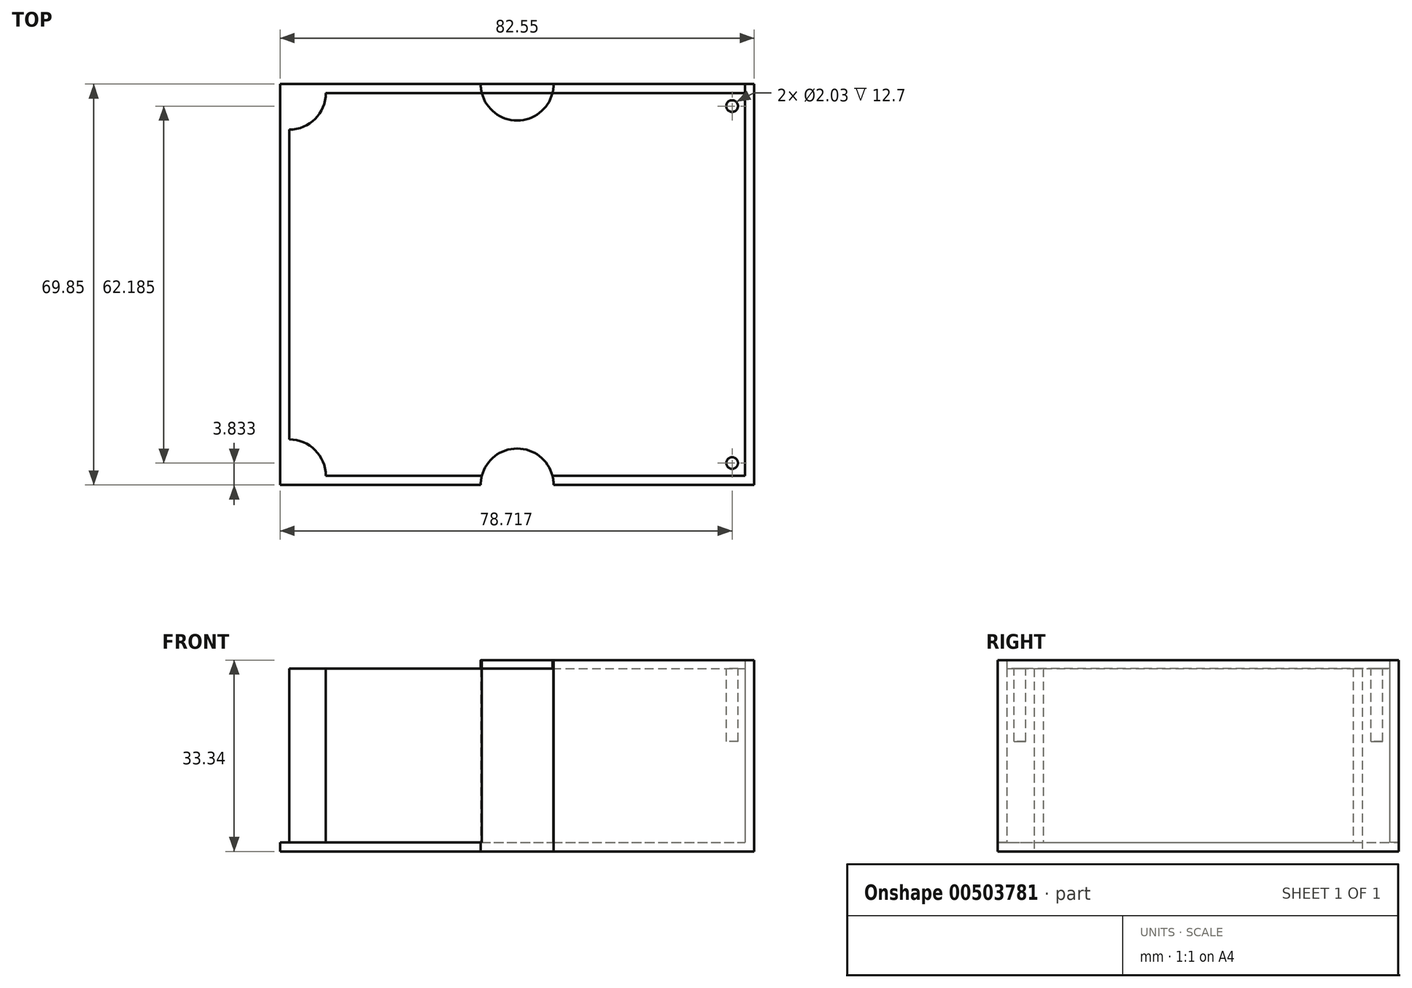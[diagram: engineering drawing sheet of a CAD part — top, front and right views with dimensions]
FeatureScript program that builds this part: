
annotation { "Feature Type Name" : "Feature", "Feature Type Description" : "" }
export const myFeature = defineFeature(function(context is Context, id is Id, definition is map)
    precondition{}
    {
        {
            var Q0;
            Q0=qCreatedBy(makeId("Top.planeOp"),FACE);
            var sketch = newSketch(context, id + "F0", { "sketchPlane" : qUnion([Q0])});
            skLineSegment(sketch, "E0.bottom", {"start": v(0, 0) * mm, "end": v(82.55, 0) * mm});
            skLineSegment(sketch, "E0.top", {"start": v(0, 69.85) * mm, "end": v(82.55, 69.85) * mm});
            skLineSegment(sketch, "E0.left", {"start": v(0, 0) * mm, "end": v(0, 69.85) * mm});
            skLineSegment(sketch, "E0.right", {"start": v(82.55, 0) * mm, "end": v(82.55, 69.85) * mm});
            skCircle(sketch, "E1", {"center": v(41.27, 0) * mm, "radius": 6.35 * mm});
            skCircle(sketch, "E2", {"center": v(41.27, 69.85) * mm, "radius": 6.35 * mm});
            skLineSegment(sketch, "E3", {"start": v(41.27, 69.85) * mm, "end": v(41.27, 76.2) * mm, "construction": true});
            skCircle(sketch, "E4", {"center": v(41.27, 73.02) * mm, "radius": 1.78 * mm});
            skLineSegment(sketch, "E5", {"start": v(41.27, 0) * mm, "end": v(41.27, -6.35) * mm, "construction": true});
            skCircle(sketch, "E6", {"center": v(41.27, -3.18) * mm, "radius": 1.78 * mm});
            skSolve(sketch);
        }
        {
            var Q0;
            Q0=makeQuery(id+"F0.imprint","IMPRINT",FACE,{"disambiguationData":[TD([[makeQuery(id+"F0.imprint","IMPRINT",EDGE,{"derivedFrom":sQuery(id+"F0.wireOp",EDGE,"E0.bottom")}),1.0]])]});
            var Q1;
            {var subQ0=sQuery(id+"F0.wireOp",EDGE,"E2");var subQ1=sQuery(id+"F0.wireOp",EDGE,"E0.top");var subQ2=makeQuery(id+"F0.imprint","INTERSECT",VERTEX,{"disambiguationData":[OD(0.0)],"derivedFrom":[subQ1,subQ0]});Q1=makeQuery(id+"F0.imprint","IMPRINT",FACE,{"disambiguationData":[TD([[makeQuery(id+"F0.imprint","IMPRINT",EDGE,{"disambiguationData":[TD([[subQ2,-1.0]])],"derivedFrom":subQ1}),1.0]])]});}
            var Q2;
            {var subQ0=sQuery(id+"F0.wireOp",EDGE,"E2");var subQ1=sQuery(id+"F0.wireOp",EDGE,"E0.top");var subQ2=makeQuery(id+"F0.imprint","INTERSECT",VERTEX,{"disambiguationData":[OD(0.0)],"derivedFrom":[subQ1,subQ0]});Q2=makeQuery(id+"F0.imprint","IMPRINT",FACE,{"disambiguationData":[TD([[makeQuery(id+"F0.imprint","IMPRINT",EDGE,{"disambiguationData":[TD([[subQ2,-1.0]])],"derivedFrom":subQ1}),-1.0]])]});}
            var Q3;
            {var subQ0=sQuery(id+"F0.wireOp",EDGE,"E1");var subQ1=sQuery(id+"F0.wireOp",EDGE,"E0.bottom");var subQ2=makeQuery(id+"F0.imprint","INTERSECT",VERTEX,{"disambiguationData":[OD(0.0)],"derivedFrom":[subQ1,subQ0]});Q3=makeQuery(id+"F0.imprint","IMPRINT",FACE,{"disambiguationData":[TD([[makeQuery(id+"F0.imprint","IMPRINT",EDGE,{"disambiguationData":[TD([[subQ2,-1.0]])],"derivedFrom":subQ1}),1.0]])]});}
            var Q4;
            {var subQ0=sQuery(id+"F0.wireOp",EDGE,"E1");var subQ1=sQuery(id+"F0.wireOp",EDGE,"E0.bottom");var subQ2=makeQuery(id+"F0.imprint","INTERSECT",VERTEX,{"disambiguationData":[OD(0.0)],"derivedFrom":[subQ1,subQ0]});Q4=makeQuery(id+"F0.imprint","IMPRINT",FACE,{"disambiguationData":[TD([[makeQuery(id+"F0.imprint","IMPRINT",EDGE,{"disambiguationData":[TD([[subQ2,-1.0]])],"derivedFrom":subQ1}),-1.0]])]});}
            extrude(context, id + "F1", {"entities" : qUnion([Q0, Q1, Q2, Q3, Q4]), "depth" : 1.59 * mm});
        }
        {
            var Q0;
            Q0=makeQuery(id+"F1.opExtrude","CAP_FACE",FACE,{"disambiguationData":[OSD([sQuery(id+"F0.wireOp",EDGE,"E0.bottom"),sQuery(id+"F0.wireOp",EDGE,"E0.top"),sQuery(id+"F0.wireOp",EDGE,"E0.left"),sQuery(id+"F0.wireOp",EDGE,"E0.right")])],"isStart":false});
            var sketch = newSketch(context, id + "F2", { "sketchPlane" : qUnion([Q0])});
            skLineSegment(sketch, "E7.bottom", {"start": v(82.55, 69.85) * mm, "end": v(80.96, 69.85) * mm});
            skLineSegment(sketch, "E7.top", {"start": v(82.55, 0) * mm, "end": v(80.96, 0) * mm});
            skLineSegment(sketch, "E7.left", {"start": v(82.55, 69.85) * mm, "end": v(82.55, 0) * mm});
            skLineSegment(sketch, "E7.right", {"start": v(80.96, 69.85) * mm, "end": v(80.96, 0) * mm});
            skLineSegment(sketch, "E8.bottom", {"start": v(80.96, 0) * mm, "end": v(0, 0) * mm});
            skLineSegment(sketch, "E8.top", {"start": v(80.96, 1.59) * mm, "end": v(0, 1.59) * mm});
            skLineSegment(sketch, "E8.left", {"start": v(80.96, 0) * mm, "end": v(80.96, 1.59) * mm});
            skLineSegment(sketch, "E8.right", {"start": v(0, 0) * mm, "end": v(0, 1.59) * mm});
            skLineSegment(sketch, "E9.bottom", {"start": v(0, 1.59) * mm, "end": v(1.59, 1.59) * mm});
            skLineSegment(sketch, "E9.top", {"start": v(0, 69.85) * mm, "end": v(1.59, 69.85) * mm});
            skLineSegment(sketch, "E9.left", {"start": v(0, 1.59) * mm, "end": v(0, 69.85) * mm});
            skLineSegment(sketch, "E9.right", {"start": v(1.59, 1.59) * mm, "end": v(1.59, 69.85) * mm});
            skLineSegment(sketch, "E10.bottom", {"start": v(1.59, 69.85) * mm, "end": v(80.96, 69.85) * mm});
            skLineSegment(sketch, "E10.top", {"start": v(1.59, 68.26) * mm, "end": v(80.96, 68.26) * mm});
            skLineSegment(sketch, "E10.left", {"start": v(1.59, 69.85) * mm, "end": v(1.59, 68.26) * mm});
            skLineSegment(sketch, "E10.right", {"start": v(80.96, 69.85) * mm, "end": v(80.96, 68.26) * mm});
            skArc(sketch, "E11", {"start": v(1.59, 7.94) * mm, "mid": v(6.08, 6.08) * mm, "end": v(7.94, 1.59) * mm});
            skArc(sketch, "E12", {"start": v(7.94, 68.26) * mm, "mid": v(6.08, 63.77) * mm, "end": v(1.59, 61.91) * mm});
            skArc(sketch, "E13", {"start": v(74.61, 68.26) * mm, "mid": v(76.47, 63.77) * mm, "end": v(80.96, 61.91) * mm});
            skArc(sketch, "E14", {"start": v(80.96, 7.94) * mm, "mid": v(76.47, 6.08) * mm, "end": v(74.61, 1.59) * mm});
            skSolve(sketch);
        }
        {
            var Q0;
            Q0=makeQuery(id+"F2.imprint","IMPRINT",FACE,{"disambiguationData":[TD([[makeQuery(id+"F2.imprint","IMPRINT",EDGE,{"derivedFrom":sQuery(id+"F2.wireOp",EDGE,"E9.bottom")}),1.0]])]});
            var Q1;
            Q1=makeQuery(id+"F2.imprint","IMPRINT",FACE,{"disambiguationData":[TD([[makeQuery(id+"F2.imprint","IMPRINT",EDGE,{"derivedFrom":sQuery(id+"F2.wireOp",EDGE,"E8.bottom")}),1.0]])]});
            var Q2;
            Q2=makeQuery(id+"F2.imprint","IMPRINT",FACE,{"disambiguationData":[TD([[makeQuery(id+"F2.imprint","IMPRINT",EDGE,{"derivedFrom":sQuery(id+"F2.wireOp",EDGE,"E7.bottom")}),-1.0]])]});
            var Q3;
            Q3=makeQuery(id+"F2.imprint","IMPRINT",FACE,{"disambiguationData":[TD([[makeQuery(id+"F2.imprint","IMPRINT",EDGE,{"derivedFrom":sQuery(id+"F2.wireOp",EDGE,"E10.bottom")}),-1.0]])]});
            extrude(context, id + "F3", {"entities" : qUnion([Q0, Q1, Q2, Q3]), "operationType" : NewBodyOperationType.ADD, "depth" : 31.75 * mm});
        }
        {
            var Q0;
            Q0=makeQuery(id+"F1.opExtrude","CAP_FACE",FACE,{"disambiguationData":[OSD([sQuery(id+"F0.wireOp",EDGE,"E0.bottom"),sQuery(id+"F0.wireOp",EDGE,"E0.top"),sQuery(id+"F0.wireOp",EDGE,"E0.left"),sQuery(id+"F0.wireOp",EDGE,"E0.right")])],"isStart":false});
            var sketch = newSketch(context, id + "F4", { "sketchPlane" : qUnion([Q0])});
            skLineSegment(sketch, "E15.bottom", {"start": v(77.22, 13.46) * mm, "end": v(80.2, 13.46) * mm, "construction": true});
            skLineSegment(sketch, "E15.top", {"start": v(77.22, 10.48) * mm, "end": v(80.2, 10.48) * mm, "construction": true});
            skLineSegment(sketch, "E15.left", {"start": v(77.22, 13.46) * mm, "end": v(77.22, 10.48) * mm, "construction": true});
            skLineSegment(sketch, "E15.right", {"start": v(80.2, 13.46) * mm, "end": v(80.2, 10.48) * mm, "construction": true});
            skCircle(sketch, "E16", {"center": v(77.22, 13.46) * mm, "radius": 1.02 * mm});
            skCircle(sketch, "E17", {"center": v(77.22, 13.46) * mm, "radius": 2.92 * mm});
            skLineSegment(sketch, "E18.bottom", {"start": v(77.22, 13.46) * mm, "end": v(10.54, 13.46) * mm, "construction": true});
            skLineSegment(sketch, "E18.top", {"start": v(77.22, 54.48) * mm, "end": v(10.54, 54.48) * mm, "construction": true});
            skLineSegment(sketch, "E18.left", {"start": v(77.22, 13.46) * mm, "end": v(77.22, 54.48) * mm, "construction": true});
            skLineSegment(sketch, "E18.right", {"start": v(10.54, 13.46) * mm, "end": v(10.54, 54.48) * mm, "construction": true});
            skCircle(sketch, "E19", {"center": v(10.54, 54.48) * mm, "radius": 2.92 * mm});
            skCircle(sketch, "E20", {"center": v(77.22, 54.48) * mm, "radius": 1.02 * mm});
            skCircle(sketch, "E21", {"center": v(77.22, 54.48) * mm, "radius": 2.92 * mm});
            skCircle(sketch, "E22", {"center": v(10.54, 13.46) * mm, "radius": 2.92 * mm});
            skLineSegment(sketch, "E23.bottom", {"start": v(80.2, 10.48) * mm, "end": v(34.99, 10.48) * mm, "construction": true});
            skLineSegment(sketch, "E23.top", {"start": v(80.2, 57.47) * mm, "end": v(34.99, 57.47) * mm, "construction": true});
            skLineSegment(sketch, "E23.left", {"start": v(80.2, 10.48) * mm, "end": v(80.2, 57.47) * mm, "construction": true});
            skLineSegment(sketch, "E23.right", {"start": v(34.99, 10.48) * mm, "end": v(34.99, 57.47) * mm, "construction": true});
            skLineSegment(sketch, "E24.bottom", {"start": v(80.96, 1.59) * mm, "end": v(80.2, 1.59) * mm, "construction": true});
            skLineSegment(sketch, "E24.top", {"start": v(80.96, 10.48) * mm, "end": v(80.2, 10.48) * mm, "construction": true});
            skLineSegment(sketch, "E24.left", {"start": v(80.96, 1.59) * mm, "end": v(80.96, 10.48) * mm, "construction": true});
            skLineSegment(sketch, "E24.right", {"start": v(80.2, 1.59) * mm, "end": v(80.2, 10.48) * mm, "construction": true});
            skCircle(sketch, "E25", {"center": v(10.54, 54.48) * mm, "radius": 1.02 * mm});
            skCircle(sketch, "E26", {"center": v(10.54, 13.46) * mm, "radius": 1.02 * mm});
            skSolve(sketch);
        }
        {
            var Q0;
            Q0=makeQuery(id+"F4.imprint","IMPRINT",FACE,{"disambiguationData":[TD([[makeQuery(id+"F4.imprint","IMPRINT",EDGE,{"derivedFrom":sQuery(id+"F4.wireOp",EDGE,"E22")}),1.0]])]});
            var Q1;
            Q1=makeQuery(id+"F4.imprint","IMPRINT",FACE,{"disambiguationData":[TD([[makeQuery(id+"F4.imprint","IMPRINT",EDGE,{"derivedFrom":sQuery(id+"F4.wireOp",EDGE,"E16")}),-1.0]])]});
            var Q2;
            Q2=makeQuery(id+"F4.imprint","IMPRINT",FACE,{"disambiguationData":[TD([[makeQuery(id+"F4.imprint","IMPRINT",EDGE,{"derivedFrom":sQuery(id+"F4.wireOp",EDGE,"E19")}),1.0]])]});
            var Q3;
            Q3=makeQuery(id+"F4.imprint","IMPRINT",FACE,{"disambiguationData":[TD([[makeQuery(id+"F4.imprint","IMPRINT",EDGE,{"derivedFrom":sQuery(id+"F4.wireOp",EDGE,"E20")}),-1.0]])]});
            extrude(context, id + "F5", {"entities" : qUnion([Q0, Q1, Q2, Q3]), "operationType" : NewBodyOperationType.ADD, "depth" : 7.62 * mm});
        }
        {
            var Q0;
            {var subQ3=sQuery(id+"F2.wireOp",EDGE,"E12");Q0=makeQuery(id+"F2.imprint","IMPRINT",FACE,{"disambiguationData":[TD([[makeQuery(id+"F2.imprint","IMPRINT",EDGE,{"derivedFrom":subQ3}),-1.0]])]});}
            var Q1;
            {var subQ3=sQuery(id+"F2.wireOp",EDGE,"E13");Q1=makeQuery(id+"F2.imprint","IMPRINT",FACE,{"disambiguationData":[TD([[makeQuery(id+"F2.imprint","IMPRINT",EDGE,{"derivedFrom":subQ3}),1.0]])]});}
            var Q2;
            {var subQ3=sQuery(id+"F2.wireOp",EDGE,"E11");Q2=makeQuery(id+"F2.imprint","IMPRINT",FACE,{"disambiguationData":[TD([[makeQuery(id+"F2.imprint","IMPRINT",EDGE,{"derivedFrom":subQ3}),-1.0]])]});}
            var Q3;
            {var subQ3=sQuery(id+"F2.wireOp",EDGE,"E14");Q3=makeQuery(id+"F2.imprint","IMPRINT",FACE,{"disambiguationData":[TD([[makeQuery(id+"F2.imprint","IMPRINT",EDGE,{"derivedFrom":subQ3}),1.0]])]});}
            extrude(context, id + "F6", {"entities" : qUnion([Q0, Q1, Q2, Q3]), "operationType" : NewBodyOperationType.ADD, "depth" : 30.29 * mm});
        }
        {
            var Q0;
            Q0=makeQuery(id+"F6.opExtrude","CAP_FACE",FACE,{"disambiguationData":[OSD([sQuery(id+"F2.wireOp",EDGE,"E8.top"),sQuery(id+"F2.wireOp",EDGE,"E9.right"),sQuery(id+"F2.wireOp",EDGE,"E11")])],"isStart":false});
            var sketch = newSketch(context, id + "F7", { "sketchPlane" : qUnion([Q0])});
            skLineSegment(sketch, "E27", {"start": v(1.59, 1.59) * mm, "end": v(6.08, 6.08) * mm, "construction": true});
            skCircle(sketch, "E28", {"center": v(3.83, 3.83) * mm, "radius": 1.02 * mm});
            skSolve(sketch);
        }
        {
            var Q0;
            Q0=makeQuery(id+"F6.opExtrude","CAP_FACE",FACE,{"disambiguationData":[OSD([sQuery(id+"F2.wireOp",EDGE,"E7.right"),sQuery(id+"F2.wireOp",EDGE,"E8.top"),sQuery(id+"F2.wireOp",EDGE,"E14")])],"isStart":false});
            var sketch = newSketch(context, id + "F8", { "sketchPlane" : qUnion([Q0])});
            skLineSegment(sketch, "E29", {"start": v(80.96, 1.59) * mm, "end": v(76.47, 6.08) * mm, "construction": true});
            skCircle(sketch, "E30", {"center": v(78.72, 3.83) * mm, "radius": 1.02 * mm});
            skSolve(sketch);
        }
        {
            var Q0;
            Q0=makeQuery(id+"F8.imprint","IMPRINT",FACE,{"disambiguationData":[TD([[makeQuery(id+"F8.imprint","IMPRINT",EDGE,{"derivedFrom":sQuery(id+"F8.wireOp",EDGE,"E30")}),1.0]])]});
            extrude(context, id + "F9", {"entities" : qUnion([Q0]), "operationType" : NewBodyOperationType.REMOVE, "oppositeDirection" : true, "depth" : 12.7 * mm});
        }
        {
            var Q0;
            Q0=makeQuery(id+"F7.imprint","IMPRINT",FACE,{"disambiguationData":[TD([[makeQuery(id+"F7.imprint","IMPRINT",EDGE,{"derivedFrom":sQuery(id+"F7.wireOp",EDGE,"E28")}),1.0]])]});
            extrude(context, id + "F10", {"entities" : qUnion([Q0]), "operationType" : NewBodyOperationType.REMOVE, "oppositeDirection" : true, "depth" : 12.7 * mm});
        }
        {
            var Q0;
            Q0=makeQuery(id+"F6.opExtrude","CAP_FACE",FACE,{"disambiguationData":[OSD([sQuery(id+"F2.wireOp",EDGE,"E9.right"),sQuery(id+"F2.wireOp",EDGE,"E10.top"),sQuery(id+"F2.wireOp",EDGE,"E12")])],"isStart":false});
            var sketch = newSketch(context, id + "F11", { "sketchPlane" : qUnion([Q0])});
            skLineSegment(sketch, "E31", {"start": v(1.59, 68.26) * mm, "end": v(6.08, 63.77) * mm, "construction": true});
            skCircle(sketch, "E32", {"center": v(3.83, 66.02) * mm, "radius": 1.02 * mm});
            skSolve(sketch);
        }
        {
            var Q0;
            Q0 = qSketchRegion(id + "F11", true);
            extrude(context, id + "F12", {"entities" : qUnion([Q0]), "operationType" : NewBodyOperationType.REMOVE, "oppositeDirection" : true, "depth" : 12.7 * mm});
        }
        {
            var Q0;
            Q0=makeQuery(id+"F6.opExtrude","CAP_FACE",FACE,{"disambiguationData":[OSD([sQuery(id+"F2.wireOp",EDGE,"E7.right"),sQuery(id+"F2.wireOp",EDGE,"E10.top"),sQuery(id+"F2.wireOp",EDGE,"E13")])],"isStart":false});
            var sketch = newSketch(context, id + "F13", { "sketchPlane" : qUnion([Q0])});
            skLineSegment(sketch, "E33", {"start": v(80.96, 68.26) * mm, "end": v(76.47, 63.77) * mm, "construction": true});
            skCircle(sketch, "E34", {"center": v(78.72, 66.02) * mm, "radius": 1.02 * mm});
            skSolve(sketch);
        }
        {
            var Q0;
            Q0 = qSketchRegion(id + "F13", true);
            var Q1;
            Q1=makeQuery(id+"F13.imprint","IMPRINT",FACE,{"disambiguationData":[TD([[makeQuery(id+"F13.imprint","IMPRINT",EDGE,{"derivedFrom":sQuery(id+"F13.wireOp",EDGE,"E34")}),1.0]])]});
            extrude(context, id + "F14", {"entities" : qUnion([Q0, Q1]), "operationType" : NewBodyOperationType.REMOVE, "oppositeDirection" : true, "depth" : 12.7 * mm});
        }
    });
